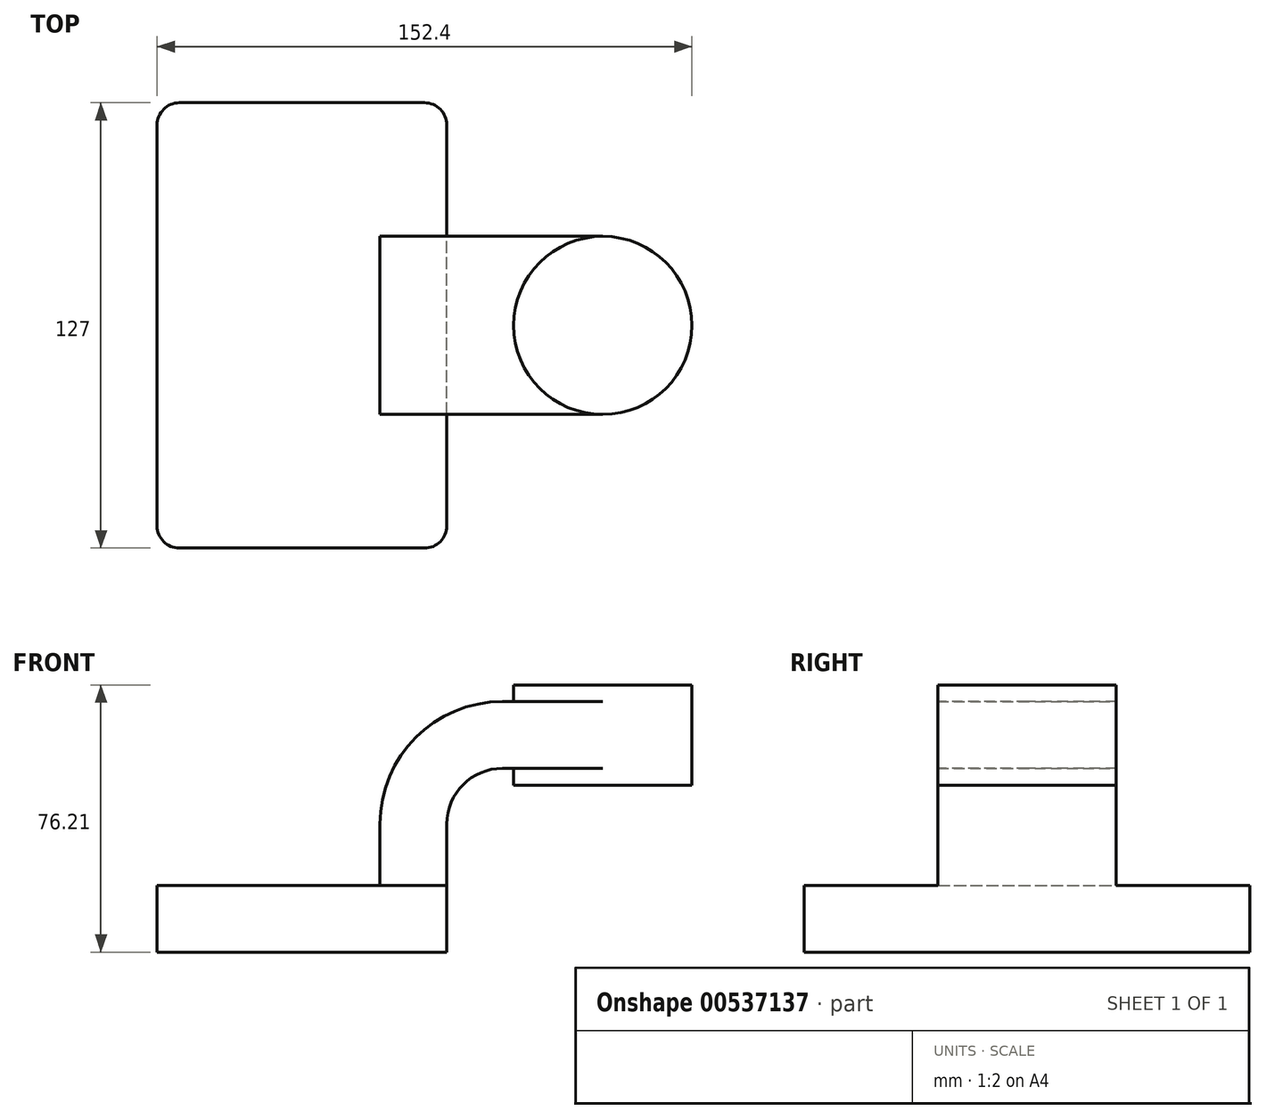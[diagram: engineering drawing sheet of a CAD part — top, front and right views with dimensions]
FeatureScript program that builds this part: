
annotation { "Feature Type Name" : "Feature", "Feature Type Description" : "" }
export const myFeature = defineFeature(function(context is Context, id is Id, definition is map)
    precondition{}
    {
        {
            var Q0;
            Q0=qCreatedBy(makeId("Front.planeOp"),FACE);
            var sketch = newSketch(context, id + "F0", { "sketchPlane" : qUnion([Q0])});
            skLineSegment(sketch, "E0.bottom", {"start": v(-41.28, -9.53) * mm, "end": v(41.28, -9.53) * mm});
            skLineSegment(sketch, "E0.top", {"start": v(-41.28, 9.52) * mm, "end": v(41.28, 9.52) * mm});
            skLineSegment(sketch, "E0.left", {"start": v(-41.28, -9.53) * mm, "end": v(-41.28, 9.53) * mm});
            skLineSegment(sketch, "E0.right", {"start": v(41.28, -9.53) * mm, "end": v(41.28, 9.52) * mm});
            skPoint(sketch, "E0.middle", {"position": v(0, 0) * mm});
            skLineSegment(sketch, "E1.bottom", {"start": v(111.12, 38.1) * mm, "end": v(60.32, 38.1) * mm});
            skLineSegment(sketch, "E1.top", {"start": v(111.12, 66.68) * mm, "end": v(60.32, 66.68) * mm});
            skLineSegment(sketch, "E1.left", {"start": v(111.12, 38.1) * mm, "end": v(111.12, 66.68) * mm});
            skLineSegment(sketch, "E1.right", {"start": v(60.32, 38.1) * mm, "end": v(60.32, 66.68) * mm});
            skPoint(sketch, "E1.middle", {"position": v(85.72, 52.39) * mm});
            skLineSegment(sketch, "E2", {"start": v(41.28, 9.52) * mm, "end": v(41.28, 27) * mm});
            skArc(sketch, "E3", {"start": v(41.27, 27) * mm, "mid": v(45.92, 38.23) * mm, "end": v(57.15, 42.88) * mm});
            skLineSegment(sketch, "E4", {"start": v(57.15, 42.88) * mm, "end": v(90.04, 42.88) * mm});
            skLineSegment(sketch, "E5.0", {"start": v(57.15, 61.93) * mm, "end": v(90.04, 61.93) * mm});
            skArc(sketch, "E5.1", {"start": v(22.22, 27) * mm, "mid": v(32.45, 51.7) * mm, "end": v(57.15, 61.93) * mm});
            skLineSegment(sketch, "E5.2", {"start": v(22.22, 9.52) * mm, "end": v(22.22, 27) * mm});
            skLineSegment(sketch, "E6", {"start": v(85.72, 38.1) * mm, "end": v(85.72, 66.68) * mm});
            skFitSpline(sketch, "E7", {"points": [v(-41.28, 9.52) * mm, v(57.15, 61.93) * mm], "startDerivative": vector(36.66, 141.33) * mm, "endDerivative": vector(90.2, -0.87) * mm});
            skSolve(sketch);
        }
        {
            var Q0;
            Q0=makeQuery(id+"F0.imprint","IMPRINT",FACE,{"disambiguationData":[TD([[makeQuery(id+"F0.imprint","IMPRINT",EDGE,{"derivedFrom":sQuery(id+"F0.wireOp",EDGE,"E0.bottom")}),1.0]])]});
            extrude(context, id + "F1", {"entities" : qUnion([Q0]), "endBound" : BoundingType.SYMMETRIC, "depth" : 127 * mm, "offsetDistance" : 25.4 * mm});
        }
        {
            var Q0;
            {var subQ1=sQuery(id+"F0.wireOp",EDGE,"E2");Q0=makeQuery(id+"F0.imprint","IMPRINT",FACE,{"disambiguationData":[TD([[makeQuery(id+"F0.imprint","IMPRINT",EDGE,{"derivedFrom":subQ1}),1.0]])]});}
            var Q1;
            {var subQ0=sQuery(id+"F0.wireOp",EDGE,"E4");var subQ1=sQuery(id+"F0.wireOp",EDGE,"E1.right");var subQ2=makeQuery(id+"F0.imprint","INTERSECT",VERTEX,{"derivedFrom":[subQ1,subQ0]});Q1=makeQuery(id+"F0.imprint","IMPRINT",FACE,{"disambiguationData":[TD([[makeQuery(id+"F0.imprint","IMPRINT",EDGE,{"disambiguationData":[TD([[subQ2,-1.0]])],"derivedFrom":subQ1}),-1.0]])]});}
            extrude(context, id + "F2", {"entities" : qUnion([Q0, Q1]), "operationType" : NewBodyOperationType.ADD, "endBound" : BoundingType.SYMMETRIC, "depth" : 50.8 * mm, "offsetDistance" : 25.4 * mm});
        }
        {
            var Q0;
            Q0=makeQuery(id+"F0.imprint","IMPRINT",FACE,{"disambiguationData":[TD([[makeQuery(id+"F0.imprint","IMPRINT",EDGE,{"derivedFrom":sQuery(id+"F0.wireOp",EDGE,"E5.1")}),1.0]])]});
            extrude(context, id + "F3", {"entities" : qUnion([Q0]), "operationType" : NewBodyOperationType.ADD, "endBound" : BoundingType.SYMMETRIC, "depth" : 15.88 * mm, "offsetDistance" : 25.4 * mm});
        }
        {
            var Q0;
            {var subQ4=sQuery(id+"F0.wireOp",EDGE,"E1.left");Q0=makeQuery(id+"F0.imprint","IMPRINT",FACE,{"disambiguationData":[TD([[makeQuery(id+"F0.imprint","IMPRINT",EDGE,{"derivedFrom":subQ4}),1.0]])]});}
            var Q1;
            Q1=sQuery(id+"F0.wireOp",EDGE,"E6");
            revolve(context, id + "F4", {"operationType" : NewBodyOperationType.ADD, "entities" : qUnion([Q0]), "axis" : qUnion([Q1]), "revolveType" : RevolveType.FULL});
        }
        {
            var Q0;
            Q0=makeQuery(id+"F1.opExtrude","CAP_EDGE",EDGE,{"disambiguationData":[OSD([sQuery(id+"F0.wireOp",EDGE,"E0.right")])],"isStart":false});
            var Q1;
            Q1=makeQuery(id+"F1.opExtrude","CAP_EDGE",EDGE,{"disambiguationData":[OSD([sQuery(id+"F0.wireOp",EDGE,"E0.left")])],"isStart":false});
            var Q2;
            Q2=makeQuery(id+"F1.opExtrude","CAP_EDGE",EDGE,{"disambiguationData":[OSD([sQuery(id+"F0.wireOp",EDGE,"E0.left")])],"isStart":true});
            var Q3;
            Q3=makeQuery(id+"F1.opExtrude","CAP_EDGE",EDGE,{"disambiguationData":[OSD([sQuery(id+"F0.wireOp",EDGE,"E0.right")])],"isStart":true});
            fillet(context, id + "F5", {"entities" : qUnion([Q0, Q1, Q2, Q3]), "radius" : 6.35 * mm, "tangentPropagation" : true, "allowEdgeOverflow" : false});
        }
    });
